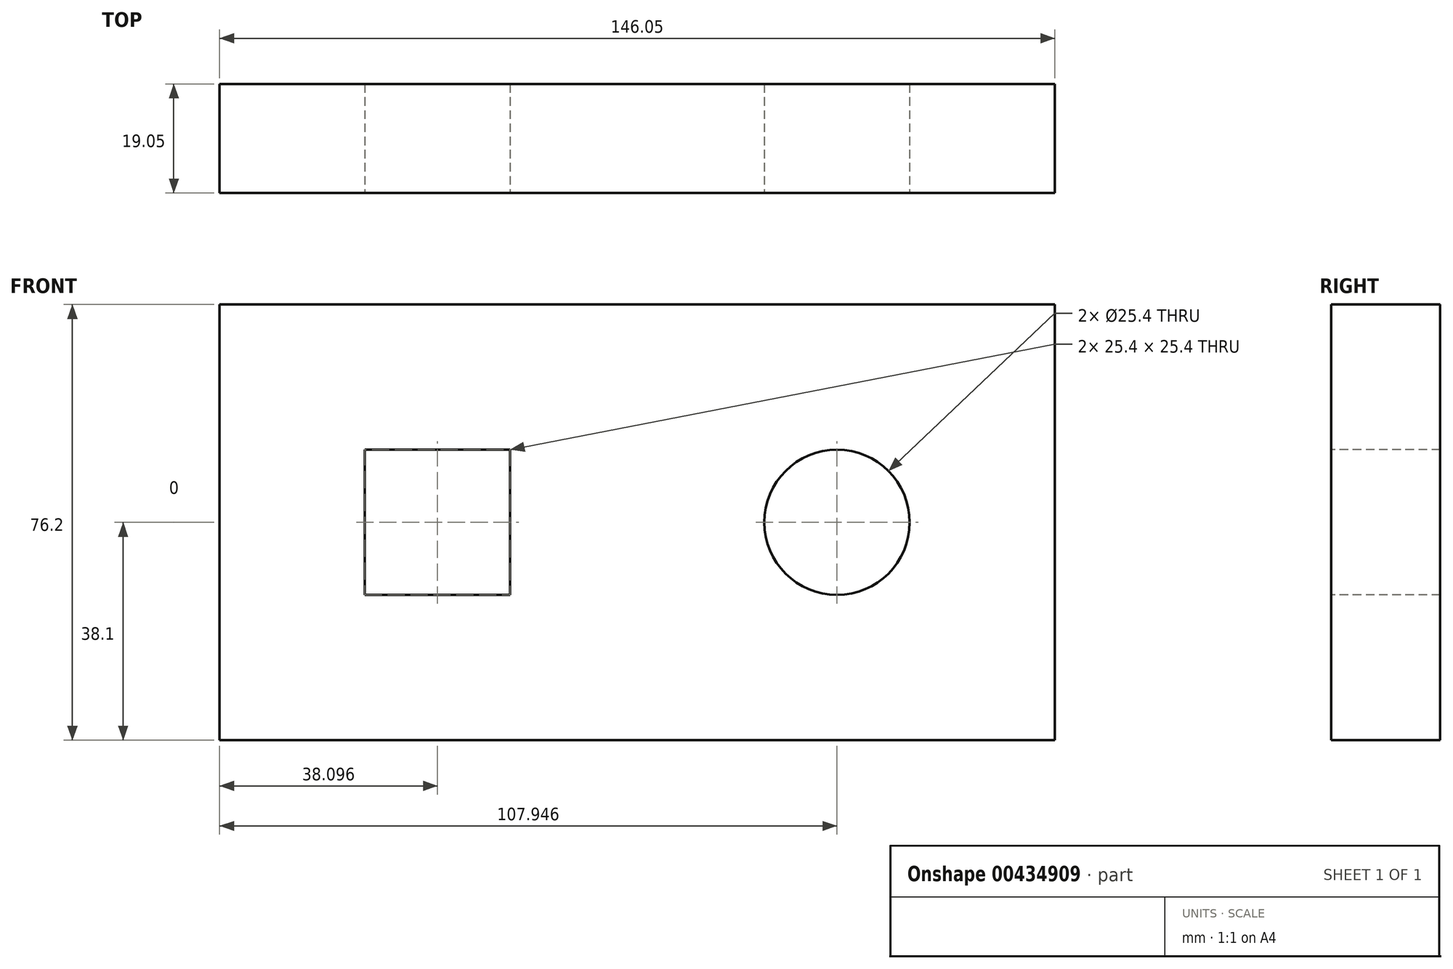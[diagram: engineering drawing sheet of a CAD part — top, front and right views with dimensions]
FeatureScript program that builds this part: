
annotation { "Feature Type Name" : "Feature", "Feature Type Description" : "" }
export const myFeature = defineFeature(function(context is Context, id is Id, definition is map)
    precondition{}
    {
        {
            var Q0;
            Q0=qCreatedBy(makeId("Front.planeOp"),FACE);
            var sketch = newSketch(context, id + "F0", { "sketchPlane" : qUnion([Q0])});
            skLineSegment(sketch, "E0", {"start": v(85.6, 0) * mm, "end": v(-60.45, 0) * mm});
            skLineSegment(sketch, "E1", {"start": v(-60.45, 0) * mm, "end": v(-60.45, 76.2) * mm});
            skLineSegment(sketch, "E2", {"start": v(-60.45, 76.2) * mm, "end": v(85.6, 76.2) * mm});
            skLineSegment(sketch, "E3", {"start": v(85.6, 76.2) * mm, "end": v(85.6, 0) * mm});
            skSolve(sketch);
        }
        {
            var Q0;
            Q0 = qSketchRegion(id + "F0", true);
            extrude(context, id + "F1", {"entities" : qUnion([Q0]), "depth" : 19.05 * mm});
        }
        {
            var Q0;
            Q0=makeQuery(id+"F1.opExtrude","CAP_FACE",FACE,{"disambiguationData":[OSD([sQuery(id+"F0.wireOp",EDGE,"E0"),sQuery(id+"F0.wireOp",EDGE,"E1"),sQuery(id+"F0.wireOp",EDGE,"E2"),sQuery(id+"F0.wireOp",EDGE,"E3")])],"isStart":false});
            var sketch = newSketch(context, id + "F2", { "sketchPlane" : qUnion([Q0])});
            skLineSegment(sketch, "E4.bottom", {"start": v(-35.05, 50.8) * mm, "end": v(-9.65, 50.8) * mm});
            skLineSegment(sketch, "E4.top", {"start": v(-35.05, 25.4) * mm, "end": v(-9.65, 25.4) * mm});
            skLineSegment(sketch, "E4.left", {"start": v(-35.05, 50.8) * mm, "end": v(-35.05, 25.4) * mm});
            skLineSegment(sketch, "E4.right", {"start": v(-9.65, 50.8) * mm, "end": v(-9.65, 25.4) * mm});
            skPoint(sketch, "E4.middle", {"position": v(-22.35, 38.1) * mm});
            skCircle(sketch, "E5", {"center": v(47.5, 38.1) * mm, "radius": 12.7 * mm});
            skSolve(sketch);
        }
        {
            var Q0;
            Q0=makeQuery(id+"F2.imprint","IMPRINT",FACE,{"disambiguationData":[TD([[makeQuery(id+"F2.imprint","IMPRINT",EDGE,{"derivedFrom":sQuery(id+"F2.wireOp",EDGE,"E5")}),1.0]])]});
            var Q1;
            Q1=makeQuery(id+"F2.imprint","IMPRINT",FACE,{"disambiguationData":[TD([[makeQuery(id+"F2.imprint","IMPRINT",EDGE,{"derivedFrom":sQuery(id+"F2.wireOp",EDGE,"E4.bottom")}),-1.0]])]});
            extrude(context, id + "F3", {"entities" : qUnion([Q0, Q1]), "operationType" : NewBodyOperationType.REMOVE, "oppositeDirection" : true, "depth" : 19.05 * mm});
        }
    });
